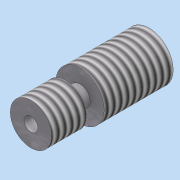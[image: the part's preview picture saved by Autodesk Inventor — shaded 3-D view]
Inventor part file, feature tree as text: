
AUTODESK INVENTOR PART (.ipt)
format: ipt  version: 2016 (Build 200138000, 138)  size: 129,024 bytes
history: native  units: mm
features: sketch x4, extrude x3, thread x2, hole x1
ambient origin geometry x8: Origin, YZ Plane, XZ Plane, XY Plane, X Axis, Y Axis, Z Axis, Center Point
bodies: Solid1 (feature_tree)
feature tree (10):
  extrude  "Extrusion1"  Depth=5.0mm TaperAngle=0.0deg
  extrude  "Extrusion2"  Depth=2.1mm TaperAngle=0.0deg
  extrude  "Extrusion3"  Depth=10.0mm TaperAngle=0.0deg
  hole  "Hole1"  [1 undecoded]
  thread  "Thread1"  [1 undecoded]
  thread  "Thread2"  [1 undecoded]
  sketch  "Sketch2"  dims[d0=6.0mm d1=5.0mm d2=0.0mm]
  sketch  "Sketch3"  dims[d3=2.95mm d4=2.1mm d5=0.0mm]
  sketch  "Sketch4"  dims[d6=7.0mm d7=10.0mm d8=0.0mm]
  sketch  "Sketch5"  dims[d9=2.0mm d10=6.0mm d11=4.0mm d12=2.0mm d13=90.0deg d14=8.0mm d15=20.594885mm d16=10.0mm d17=0.0mm d18=10.0mm d19=0.0mm]
note: 3 required parameter values undecoded (feature->parameter linkage not recoverable at this tier; creation-order binding heuristic only, values carry confidence <= 0.55)
